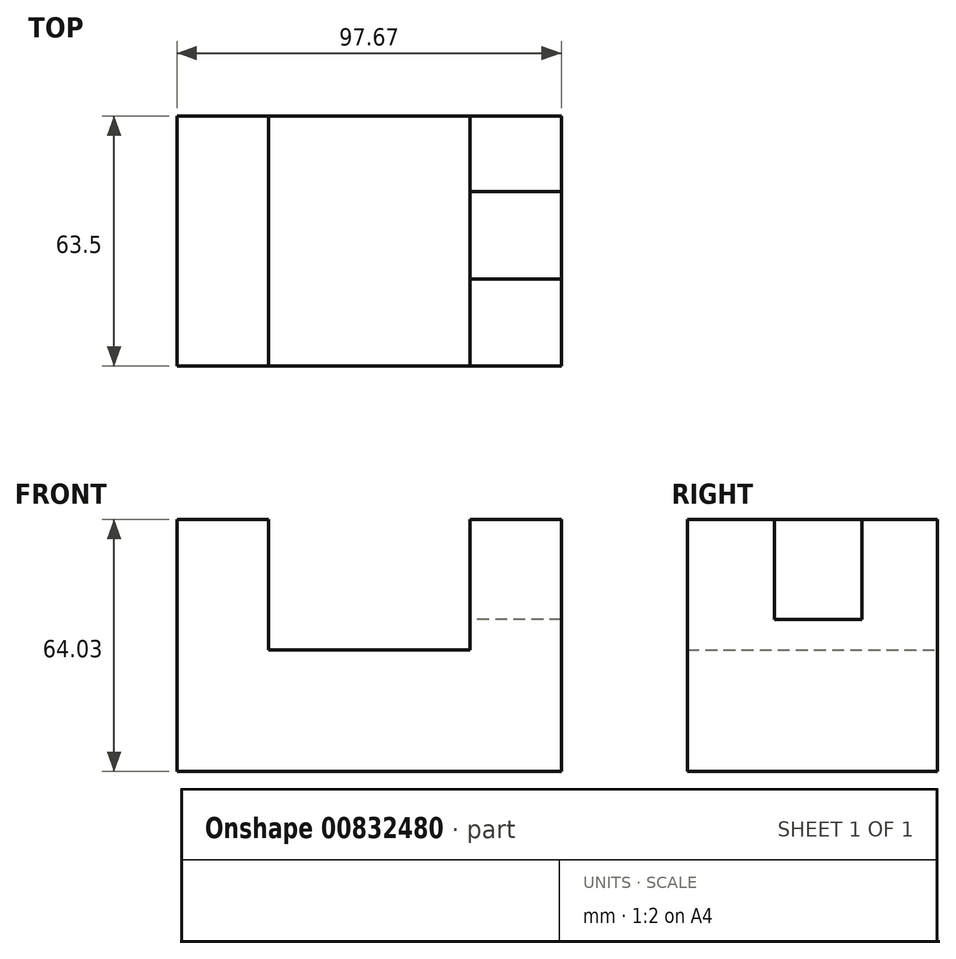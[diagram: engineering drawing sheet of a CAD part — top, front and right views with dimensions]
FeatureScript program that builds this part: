
annotation { "Feature Type Name" : "Feature", "Feature Type Description" : "" }
export const myFeature = defineFeature(function(context is Context, id is Id, definition is map)
    precondition{}
    {
        {
            var Q0;
            Q0=qCreatedBy(makeId("Front.planeOp"),FACE);
            var sketch = newSketch(context, id + "F0", { "sketchPlane" : qUnion([Q0])});
            skLineSegment(sketch, "E0.bottom", {"start": v(46.92, -26.68) * mm, "end": v(-50.75, -26.68) * mm});
            skLineSegment(sketch, "E0.top", {"start": v(46.92, 37.35) * mm, "end": v(23.67, 37.35) * mm});
            skLineSegment(sketch, "E0.left", {"start": v(46.92, -26.68) * mm, "end": v(46.92, 37.35) * mm});
            skLineSegment(sketch, "E0.right", {"start": v(-50.75, -26.68) * mm, "end": v(-50.75, 37.35) * mm});
            skLineSegment(sketch, "E1.bottom", {"start": v(23.67, 4.24) * mm, "end": v(-27.5, 4.24) * mm});
            skLineSegment(sketch, "E1.left", {"start": v(23.67, 4.24) * mm, "end": v(23.67, 37.35) * mm});
            skLineSegment(sketch, "E1.right", {"start": v(-27.5, 4.24) * mm, "end": v(-27.5, 37.35) * mm});
            skLineSegment(sketch, "E2.trimOffspring", {"start": v(-27.5, 37.35) * mm, "end": v(-50.75, 37.35) * mm});
            skSolve(sketch);
        }
        {
            var Q0;
            Q0 = qSketchRegion(id + "F0", true);
            extrude(context, id + "F1", {"entities" : qUnion([Q0]), "depth" : 63.5 * mm, "offsetDistance" : 25.4 * mm});
        }
        {
            var Q0;
            Q0=makeQuery(id+"F1.opExtrude","SWEPT_FACE",FACE,{"disambiguationData":[OSD([sQuery(id+"F0.wireOp",EDGE,"E0.top")])]});
            var sketch = newSketch(context, id + "F2", { "sketchPlane" : qUnion([Q0])});
            skLineSegment(sketch, "E3.bottom", {"start": v(46.92, -41.42) * mm, "end": v(23.67, -41.42) * mm});
            skLineSegment(sketch, "E3.top", {"start": v(46.92, -19.16) * mm, "end": v(23.67, -19.16) * mm});
            skLineSegment(sketch, "E3.left", {"start": v(46.92, -41.42) * mm, "end": v(46.92, -19.16) * mm});
            skLineSegment(sketch, "E3.right", {"start": v(23.67, -41.42) * mm, "end": v(23.67, -19.16) * mm});
            skSolve(sketch);
        }
        {
            var Q0;
            Q0 = qSketchRegion(id + "F2", true);
            extrude(context, id + "F3", {"entities" : qUnion([Q0]), "operationType" : NewBodyOperationType.REMOVE, "oppositeDirection" : true, "depth" : 25.4 * mm, "offsetDistance" : 25.4 * mm});
        }
    });
